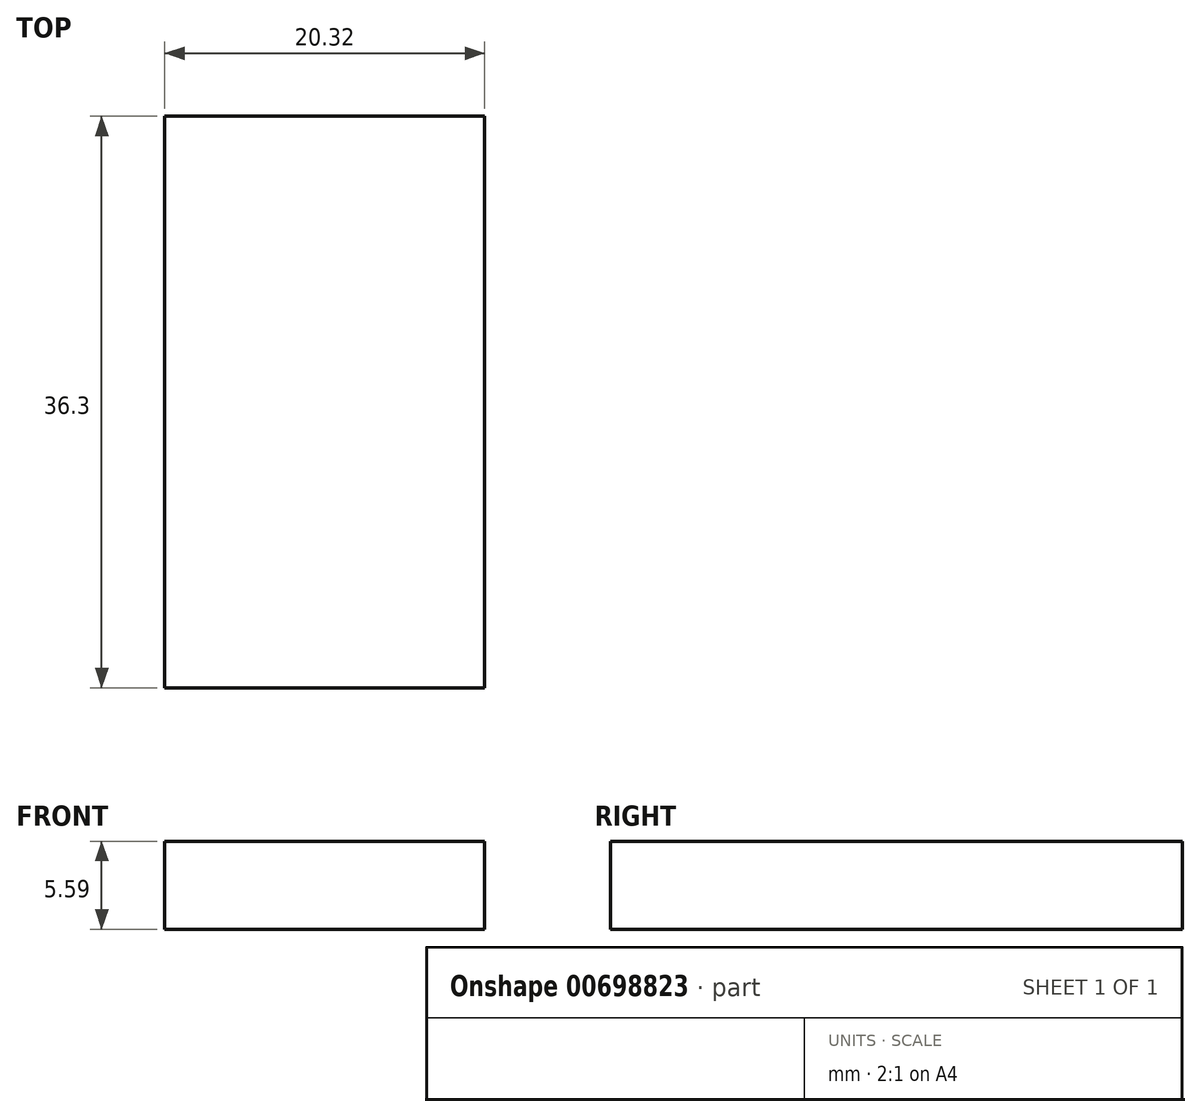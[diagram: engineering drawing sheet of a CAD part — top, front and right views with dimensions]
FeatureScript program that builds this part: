
annotation { "Feature Type Name" : "Feature", "Feature Type Description" : "" }
export const myFeature = defineFeature(function(context is Context, id is Id, definition is map)
    precondition{}
    {
        {
            var Q0;
            Q0=qCreatedBy(makeId("Top.planeOp"),FACE);
            var sketch = newSketch(context, id + "F0", { "sketchPlane" : qUnion([Q0])});
            skLineSegment(sketch, "E0.bottom", {"start": v(0, 0) * mm, "end": v(-20.32, 0) * mm});
            skLineSegment(sketch, "E0.top", {"start": v(0, -36.3) * mm, "end": v(-20.32, -36.3) * mm});
            skLineSegment(sketch, "E0.left", {"start": v(0, 0) * mm, "end": v(0, -36.3) * mm});
            skLineSegment(sketch, "E0.right", {"start": v(-20.32, 0) * mm, "end": v(-20.32, -36.3) * mm});
            skLineSegment(sketch, "E1.bottom", {"start": v(-20.32, 0) * mm, "end": v(0, 0) * mm});
            skLineSegment(sketch, "E1.top", {"start": v(-20.32, 6.35) * mm, "end": v(0, 6.35) * mm});
            skLineSegment(sketch, "E1.left", {"start": v(-20.32, 0) * mm, "end": v(-20.32, 6.35) * mm});
            skLineSegment(sketch, "E1.right", {"start": v(0, 0) * mm, "end": v(0, 6.35) * mm});
            skLineSegment(sketch, "E2.bottom", {"start": v(0, 0) * mm, "end": v(6.35, 0) * mm});
            skLineSegment(sketch, "E2.top", {"start": v(0, -36.5) * mm, "end": v(6.35, -36.5) * mm});
            skLineSegment(sketch, "E2.left", {"start": v(0, 0) * mm, "end": v(0, -36.5) * mm});
            skLineSegment(sketch, "E2.right", {"start": v(6.35, 0) * mm, "end": v(6.35, -36.5) * mm});
            skSolve(sketch);
        }
        {
            var Q0;
            {var subQ0=sQuery(id+"F0.wireOp",EDGE,"E0.top");Q0=makeQuery(id+"F0.imprint","IMPRINT",FACE,{"disambiguationData":[TD([[makeQuery(id+"F0.imprint","IMPRINT",EDGE,{"derivedFrom":subQ0}),-1.0]])]});}
            extrude(context, id + "F1", {"entities" : qUnion([Q0]), "depth" : 5.6 * mm, "offsetDistance" : 25.4 * mm});
        }
    });
